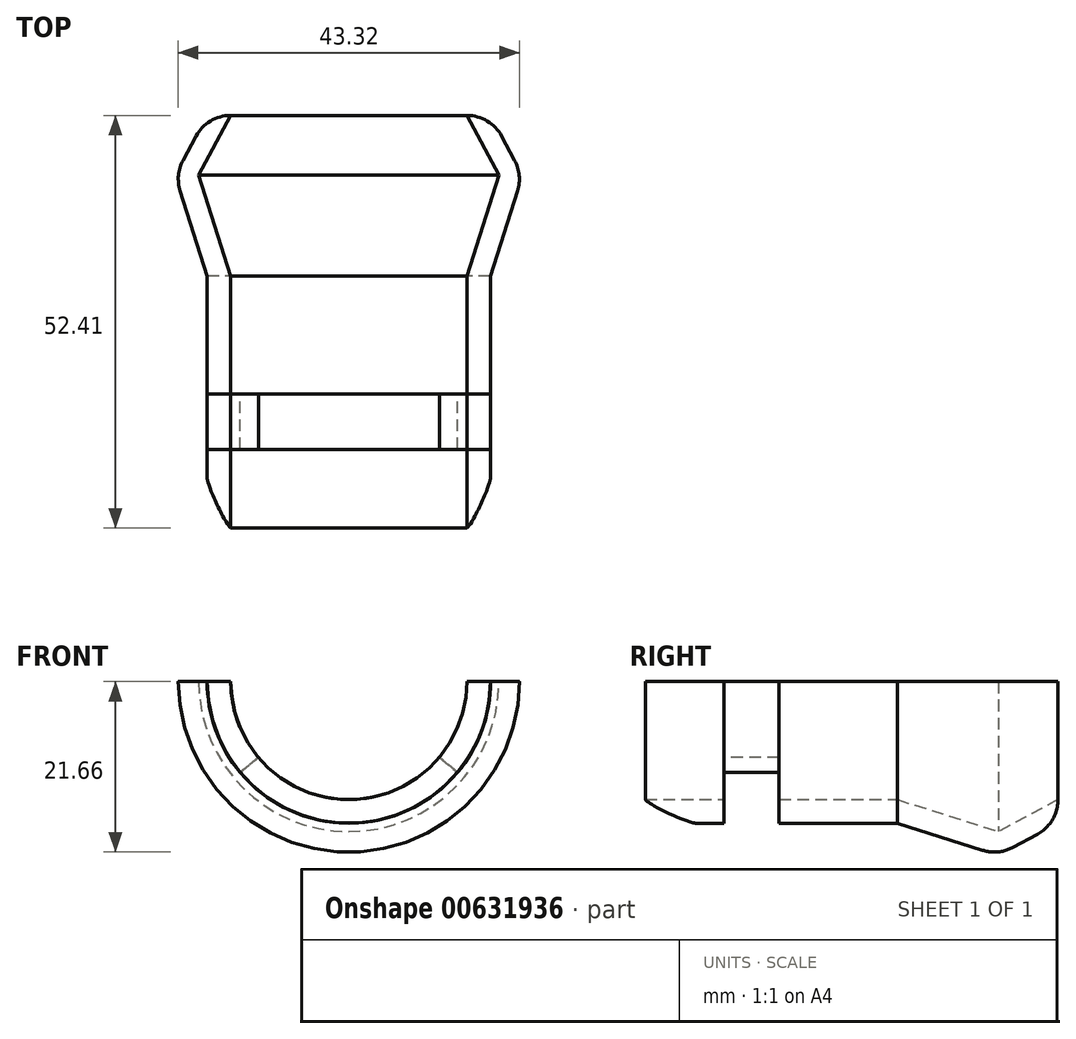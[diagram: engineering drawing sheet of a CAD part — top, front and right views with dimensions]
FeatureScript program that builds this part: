
annotation { "Feature Type Name" : "Feature", "Feature Type Description" : "" }
export const myFeature = defineFeature(function(context is Context, id is Id, definition is map)
    precondition{}
    {
        {
            var Q0;
            Q0=qCreatedBy(makeId("Top.planeOp"),FACE);
            var sketch = newSketch(context, id + "F0", { "sketchPlane" : qUnion([Q0])});
            skLineSegment(sketch, "E0", {"start": v(0, 0) * mm, "end": v(-15, 0) * mm});
            skLineSegment(sketch, "E1", {"start": v(-15, 0) * mm, "end": v(-15, 15) * mm});
            skLineSegment(sketch, "E2", {"start": v(-15, 15) * mm, "end": v(-18, 15) * mm});
            skLineSegment(sketch, "E3", {"start": v(-18, 15) * mm, "end": v(-18, 0) * mm});
            skLineSegment(sketch, "E4", {"start": v(-18, 0) * mm, "end": v(-15, 0) * mm});
            skLineSegment(sketch, "E5", {"start": v(-15, 0) * mm, "end": v(-15, -7) * mm});
            skLineSegment(sketch, "E6", {"start": v(-15, -7) * mm, "end": v(-18, -7) * mm});
            skLineSegment(sketch, "E7", {"start": v(-18, -7) * mm, "end": v(-18, 0) * mm});
            skLineSegment(sketch, "E8", {"start": v(-18, -7) * mm, "end": v(-18, -17) * mm});
            skLineSegment(sketch, "E9", {"start": v(-18, -17) * mm, "end": v(-15, -17) * mm});
            skLineSegment(sketch, "E10", {"start": v(-15, -17) * mm, "end": v(-15, -7) * mm});
            skLineSegment(sketch, "E11", {"start": v(-15, 15) * mm, "end": v(-19.07, 27.84) * mm});
            skLineSegment(sketch, "E12", {"start": v(-19.07, 27.84) * mm, "end": v(-22.07, 27.84) * mm});
            skLineSegment(sketch, "E13", {"start": v(-22.07, 27.84) * mm, "end": v(-18, 15) * mm});
            skLineSegment(sketch, "E14", {"start": v(-19.07, 27.84) * mm, "end": v(-15, 35.41) * mm});
            skLineSegment(sketch, "E15", {"start": v(-15, 35.41) * mm, "end": v(-18, 35.41) * mm});
            skLineSegment(sketch, "E16", {"start": v(-18, 35.41) * mm, "end": v(-22.07, 27.84) * mm});
            skLineSegment(sketch, "E17", {"start": v(0, 35.4) * mm, "end": v(0, -18.18) * mm});
            skLineSegment(sketch, "E18.MirrorCS", {"start": v(15, 15) * mm, "end": v(18, 15) * mm});
            skLineSegment(sketch, "E19.MirrorCS", {"start": v(18, 0) * mm, "end": v(15, 0) * mm});
            skLineSegment(sketch, "E20.MirrorCS", {"start": v(19.07, 27.84) * mm, "end": v(22.07, 27.84) * mm});
            skLineSegment(sketch, "E21.MirrorCS", {"start": v(15, -7) * mm, "end": v(18, -7) * mm});
            skLineSegment(sketch, "E22.MirrorCS", {"start": v(15, 35.41) * mm, "end": v(18, 35.41) * mm});
            skLineSegment(sketch, "E23.MirrorCS", {"start": v(18, -17) * mm, "end": v(15, -17) * mm});
            skLineSegment(sketch, "E24.MirrorCS", {"start": v(19.07, 27.84) * mm, "end": v(15, 35.41) * mm});
            skLineSegment(sketch, "E25.MirrorCS", {"start": v(18, 35.41) * mm, "end": v(22.07, 27.84) * mm});
            skLineSegment(sketch, "E26.MirrorCS", {"start": v(15, 0) * mm, "end": v(15, 15) * mm});
            skLineSegment(sketch, "E27.MirrorCS", {"start": v(18, 15) * mm, "end": v(18, 0) * mm});
            skLineSegment(sketch, "E28.MirrorCS", {"start": v(15, 15) * mm, "end": v(19.07, 27.84) * mm});
            skLineSegment(sketch, "E29.MirrorCS", {"start": v(15, -17) * mm, "end": v(15, -7) * mm});
            skLineSegment(sketch, "E30.MirrorCS", {"start": v(15, 0) * mm, "end": v(15, -7) * mm});
            skLineSegment(sketch, "E31.MirrorCS", {"start": v(22.07, 27.84) * mm, "end": v(18, 15) * mm});
            skLineSegment(sketch, "E32.MirrorCS", {"start": v(18, -7) * mm, "end": v(18, -17) * mm});
            skLineSegment(sketch, "E33.MirrorCS", {"start": v(18, -7) * mm, "end": v(18, 0) * mm});
            skSolve(sketch);
        }
        {
            var Q0;
            Q0=makeQuery(id+"F0.imprint","IMPRINT",FACE,{"disambiguationData":[TD([[makeQuery(id+"F0.imprint","IMPRINT",EDGE,{"derivedFrom":sQuery(id+"F0.wireOp",EDGE,"E12")}),-1.0]])]});
            var Q1;
            Q1=makeQuery(id+"F0.imprint","IMPRINT",FACE,{"disambiguationData":[TD([[makeQuery(id+"F0.imprint","IMPRINT",EDGE,{"derivedFrom":sQuery(id+"F0.wireOp",EDGE,"E2")}),-1.0]])]});
            var Q2;
            Q2=makeQuery(id+"F0.imprint","IMPRINT",FACE,{"disambiguationData":[TD([[makeQuery(id+"F0.imprint","IMPRINT",EDGE,{"derivedFrom":sQuery(id+"F0.wireOp",EDGE,"E1")}),1.0]])]});
            var Q3;
            Q3=makeQuery(id+"F0.imprint","IMPRINT",FACE,{"disambiguationData":[TD([[makeQuery(id+"F0.imprint","IMPRINT",EDGE,{"derivedFrom":sQuery(id+"F0.wireOp",EDGE,"E6")}),1.0]])]});
            var Q4;
            Q4=sQuery(id+"F0.wireOp",EDGE,"E17");
            revolve(context, id + "F1", {"entities" : qUnion([Q0, Q1, Q2, Q3]), "axis" : qUnion([Q4]), "revolveType" : RevolveType.ONE_DIRECTION, "angle" : 180 * degree});
        }
        {
            var Q0;
            Q0=makeQuery(id+"F0.imprint","IMPRINT",FACE,{"disambiguationData":[TD([[makeQuery(id+"F0.imprint","IMPRINT",EDGE,{"derivedFrom":sQuery(id+"F0.wireOp",EDGE,"E4")}),-1.0]])]});
            var Q1;
            Q1=sQuery(id+"F0.wireOp",EDGE,"E17");
            revolve(context, id + "F2", {"entities" : qUnion([Q0]), "axis" : qUnion([Q1]), "revolveType" : RevolveType.ONE_DIRECTION, "angle" : 40 * degree});
        }
        {
            var Q0;
            Q0=makeQuery(id+"F0.imprint","IMPRINT",FACE,{"disambiguationData":[TD([[makeQuery(id+"F0.imprint","IMPRINT",EDGE,{"derivedFrom":sQuery(id+"F0.wireOp",EDGE,"E19.MirrorCS")}),1.0]])]});
            var Q1;
            Q1=sQuery(id+"F0.wireOp",EDGE,"E17");
            revolve(context, id + "F3", {"entities" : qUnion([Q0]), "axis" : qUnion([Q1]), "revolveType" : RevolveType.ONE_DIRECTION, "oppositeDirection" : true, "angle" : 40 * degree});
        }
        {
            var Q0;
            Q0=makeQuery(id+"F1.opRevolve","SWEPT_EDGE",EDGE,{"disambiguationData":[OSD([sQuery(id+"F0.wireOp",EDGE,"E12"),sQuery(id+"F0.wireOp",EDGE,"E13"),sQuery(id+"F0.wireOp",EDGE,"E16")])]});
            fillet(context, id + "F4", {"entities" : qUnion([Q0]), "radius" : 5 * mm, "tangentPropagation" : true, "allowEdgeOverflow" : false});
        }
        {
            var Q0;
            Q0=makeQuery(id+"F1.opRevolve","SWEPT_EDGE",EDGE,{"disambiguationData":[OSD([sQuery(id+"F0.wireOp",EDGE,"E8"),sQuery(id+"F0.wireOp",EDGE,"E9")])]});
            fillet(context, id + "F5", {"entities" : qUnion([Q0]), "radius" : 8.45 * mm, "rho" : .2, "crossSection" : FilletCrossSection.CONIC, "allowEdgeOverflow" : false});
        }
        {
            var Q0;
            Q0=makeQuery(id+"F1.opRevolve","SWEPT_EDGE",EDGE,{"disambiguationData":[OSD([sQuery(id+"F0.wireOp",EDGE,"E15"),sQuery(id+"F0.wireOp",EDGE,"E16")])]});
            fillet(context, id + "F6", {"entities" : qUnion([Q0]), "radius" : 5 * mm, "tangentPropagation" : true, "allowEdgeOverflow" : false});
        }
    });
